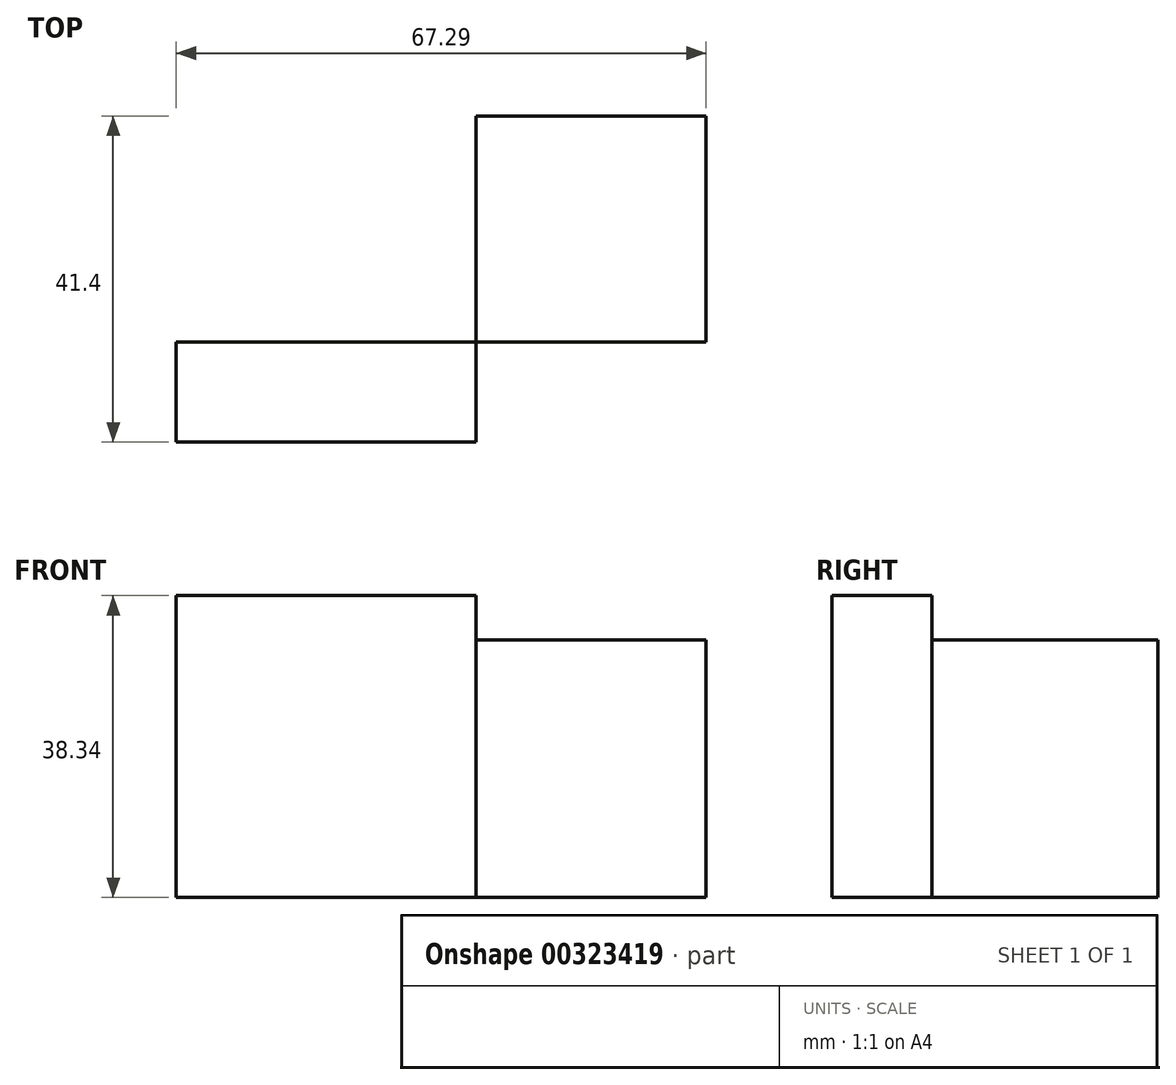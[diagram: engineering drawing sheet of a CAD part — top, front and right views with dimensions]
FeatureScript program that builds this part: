
annotation { "Feature Type Name" : "Feature", "Feature Type Description" : "" }
export const myFeature = defineFeature(function(context is Context, id is Id, definition is map)
    precondition{}
    {
        {
            var Q0;
            Q0=qCreatedBy(makeId("Front.planeOp"),FACE);
            var sketch = newSketch(context, id + "F0", { "sketchPlane" : qUnion([Q0])});
            skLineSegment(sketch, "E0", {"start": v(0, 0) * mm, "end": v(0, 32.7) * mm});
            skLineSegment(sketch, "E1", {"start": v(0, 32.7) * mm, "end": v(29.19, 32.7) * mm});
            skLineSegment(sketch, "E2", {"start": v(29.19, 32.7) * mm, "end": v(29.19, 0) * mm});
            skLineSegment(sketch, "E3", {"start": v(29.19, 0) * mm, "end": v(0, 0) * mm});
            skSolve(sketch);
        }
        {
            var Q0;
            Q0=makeQuery(id+"F0.imprint","IMPRINT",FACE,{"disambiguationData":[TD([[makeQuery(id+"F0.imprint","IMPRINT",EDGE,{"derivedFrom":sQuery(id+"F0.wireOp",EDGE,"E0")}),-1.0]])]});
            extrude(context, id + "F1", {"entities" : qUnion([Q0]), "depth" : 28.7 * mm});
        }
        {
            var Q0;
            Q0=makeQuery(id+"F1.opExtrude","CAP_FACE",FACE,{"disambiguationData":[OSD([sQuery(id+"F0.wireOp",EDGE,"E0"),sQuery(id+"F0.wireOp",EDGE,"E1"),sQuery(id+"F0.wireOp",EDGE,"E2"),sQuery(id+"F0.wireOp",EDGE,"E3")])],"isStart":false});
            var sketch = newSketch(context, id + "F2", { "sketchPlane" : qUnion([Q0])});
            skLineSegment(sketch, "E4", {"start": v(0, 0) * mm, "end": v(-38.1, 0) * mm});
            skLineSegment(sketch, "E5", {"start": v(-38.1, 0) * mm, "end": v(-38.1, 38.34) * mm});
            skLineSegment(sketch, "E6", {"start": v(-38.1, 38.34) * mm, "end": v(0, 38.34) * mm});
            skLineSegment(sketch, "E7", {"start": v(0, 38.34) * mm, "end": v(0, 0) * mm});
            skSolve(sketch);
        }
        {
            var Q0;
            {var subQ3=sQuery(id+"F2.wireOp",EDGE,"E4");Q0=makeQuery(id+"F2.imprint","IMPRINT",FACE,{"disambiguationData":[TD([[makeQuery(id+"F2.imprint","IMPRINT",EDGE,{"derivedFrom":subQ3}),-1.0]])]});}
            extrude(context, id + "F3", {"entities" : qUnion([Q0]), "depth" : 25.4 * mm});
        }
        {
            var Q0;
            Q0=makeQuery(id+"F3.opExtrude","CAP_FACE",FACE,{"disambiguationData":[OSD([sQuery(id+"F2.wireOp",EDGE,"E4"),sQuery(id+"F2.wireOp",EDGE,"E5"),sQuery(id+"F2.wireOp",EDGE,"E6"),sQuery(id+"F2.wireOp",EDGE,"E7")])],"isStart":false});
            extrude(context, id + "F4", {"entities" : qUnion([Q0]), "operationType" : NewBodyOperationType.REMOVE, "oppositeDirection" : true, "depth" : 12.7 * mm});
        }
    });
